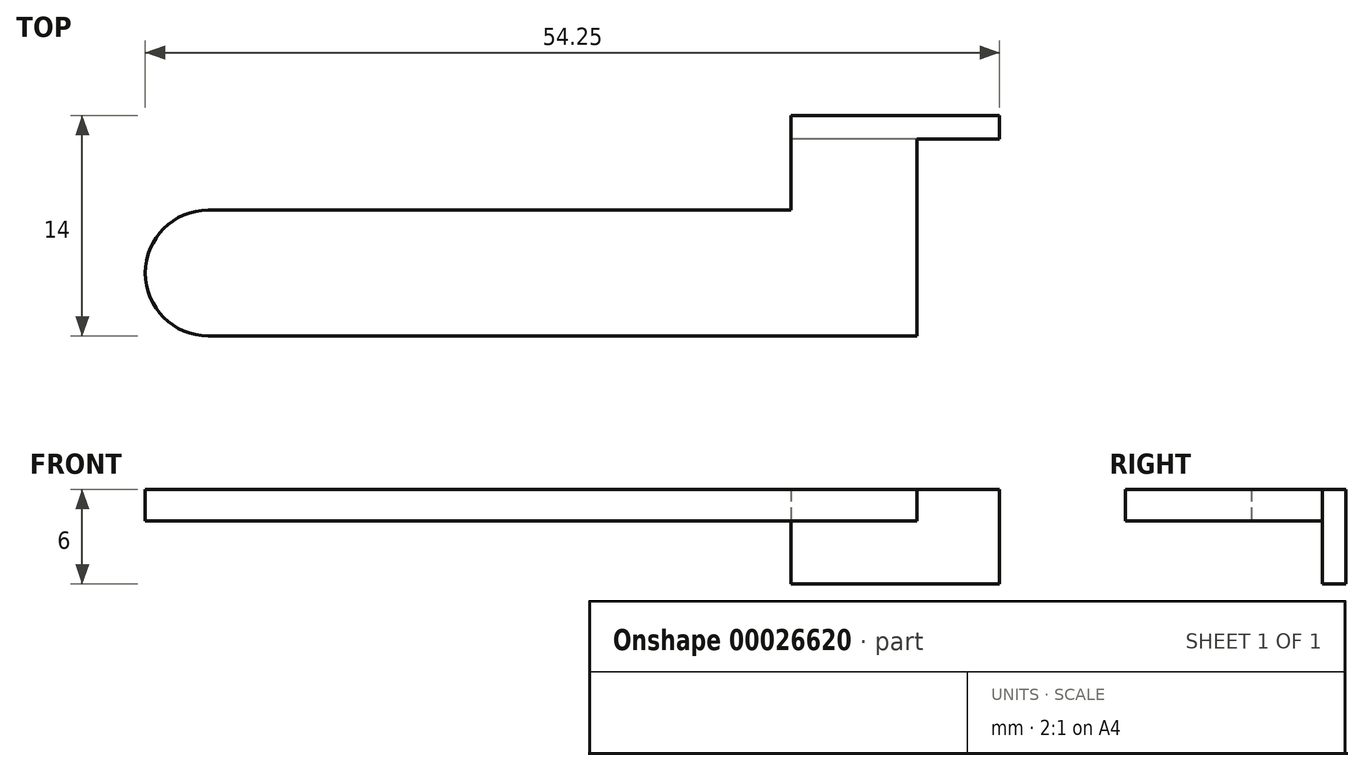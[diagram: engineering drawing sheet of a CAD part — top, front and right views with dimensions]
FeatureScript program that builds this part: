
annotation { "Feature Type Name" : "Feature", "Feature Type Description" : "" }
export const myFeature = defineFeature(function(context is Context, id is Id, definition is map)
    precondition{}
    {
        {
            var Q0;
            Q0=qCreatedBy(makeId("Top.planeOp"),FACE);
            var sketch = newSketch(context, id + "F0", { "sketchPlane" : qUnion([Q0])});
            skCircle(sketch, "E0", {"center": v(0, 0) * mm, "radius": 4 * mm});
            skLineSegment(sketch, "E1", {"start": v(0, 4) * mm, "end": v(0, -4) * mm});
            skLineSegment(sketch, "E2", {"start": v(0, -4) * mm, "end": v(45, -4) * mm});
            skLineSegment(sketch, "E3", {"start": v(45, -4) * mm, "end": v(45, 4) * mm});
            skLineSegment(sketch, "E4", {"start": v(45, 4) * mm, "end": v(0, 4) * mm});
            skLineSegment(sketch, "E5", {"start": v(45, 4) * mm, "end": v(45, 10) * mm});
            skLineSegment(sketch, "E6", {"start": v(45, 10) * mm, "end": v(37, 10) * mm});
            skLineSegment(sketch, "E7", {"start": v(37, 10) * mm, "end": v(37, 4) * mm});
            skSolve(sketch);
        }
        {
            var Q0;
            Q0=qSketchRegion(id+"F0",true);
            extrude(context, id + "F1", {"entities" : qUnion([Q0]), "depth" : 2 * mm});
        }
        {
            var Q0;
            Q0=makeQuery(id+"F1.opExtrude","SWEPT_FACE",FACE,{"disambiguationData":[OSD([sQuery(id+"F0.wireOp",EDGE,"E3"),sQuery(id+"F0.wireOp",EDGE,"E5")])]});
            var sketch = newSketch(context, id + "F2", { "sketchPlane" : qUnion([Q0])});
            skLineSegment(sketch, "E8", {"start": v(10, 2) * mm, "end": v(10, -4) * mm});
            skLineSegment(sketch, "E9", {"start": v(10, 2) * mm, "end": v(8.5, 2) * mm});
            skLineSegment(sketch, "E10", {"start": v(8.5, 2) * mm, "end": v(8.5, -4) * mm});
            skLineSegment(sketch, "E11", {"start": v(8.5, -4) * mm, "end": v(10, -4) * mm});
            skSolve(sketch);
        }
        {
            var Q0;
            Q0 = qSketchRegion(id + "F2", true);
            extrude(context, id + "F3", {"entities" : qUnion([Q0]), "operationType" : NewBodyOperationType.ADD, "depth" : 5.25 * mm, "hasSecondDirection" : true, "secondDirectionOppositeDirection" : true, "secondDirectionDepth" : 8 * mm});
        }
    });
